# Revit family: Internal block_56_160_CR
name_source: partatom
category: Оборудование
units: mm (PartAtom-declared; Revit-internal decimal feet)

## family parameters
Всегда вертикально = Да
Классификация = Нет
На основе рабочей плоскости = Нет
Общий = Нет
При загрузке вырезать с полостями = Нет
Размер круглого соединителя = Использовать диаметр
Тип детали = Нормальный
Точка принадлежности помещению = Нет

## types (9) — shared parameters
00_20_Manufacturer = BLAUBERG
00_20_Name = Internal block
Casing Material = Steel, white, mat
G = 950 мм
Grid Material = Mesh, steel, painted,  white
H = 950 мм
I = 80 мм
I1 = 10 мм
Length = 950 мм
Load Classification = HVAC
Maintenance zone material = <По категории>
Maximum Air Flow = 0.0 л/с
Weight = 24.00 кг
Width = 950 мм
Изготовитель = BLAUBERG
zero-valued in all types: Отметка по умолчанию

## per-type parameters (varying)
| type | C | Height | Power | dg | dr |
| BLHV-56-I-CR-AC/1R1A | 232 мм | 312 мм | 90 Вт | 13 мм | 6 мм |
| BLHV-71-I-CR-AC/1R1A | 232 мм | 312 мм | 180 Вт | 16 мм | 10 мм |
| BLHV-80-I-CR-AC/1R1A | 232 мм | 312 мм | 180 Вт | 16 мм | 10 мм |
| BLHV-90-I-CR-AC/1R1A | 286 мм | 366 мм | 180 Вт | 16 мм | 10 мм |
| BLHV-100-I-CR-AC/1R1A | 286 мм | 366 мм | 180 Вт | 16 мм | 10 мм |
| BLHV-112-I-CR-AC/1R1A | 286 мм | 366 мм | 180 Вт | 16 мм | 10 мм |
| BLHV-125-I-CR-AC/1R1A | 286 мм | 366 мм | 180 Вт | 16 мм | 10 мм |
| BLHV-140-I-CR-AC/1R1A | 286 мм | 366 мм | 270 Вт | 16 мм | 10 мм |
| BLHV-160-I-CR-AC/1R1A | 286 мм | 366 мм | 270 Вт | 16 мм | 10 мм |

note: column(s) folded — value = type name in every type: 00_20_Type
